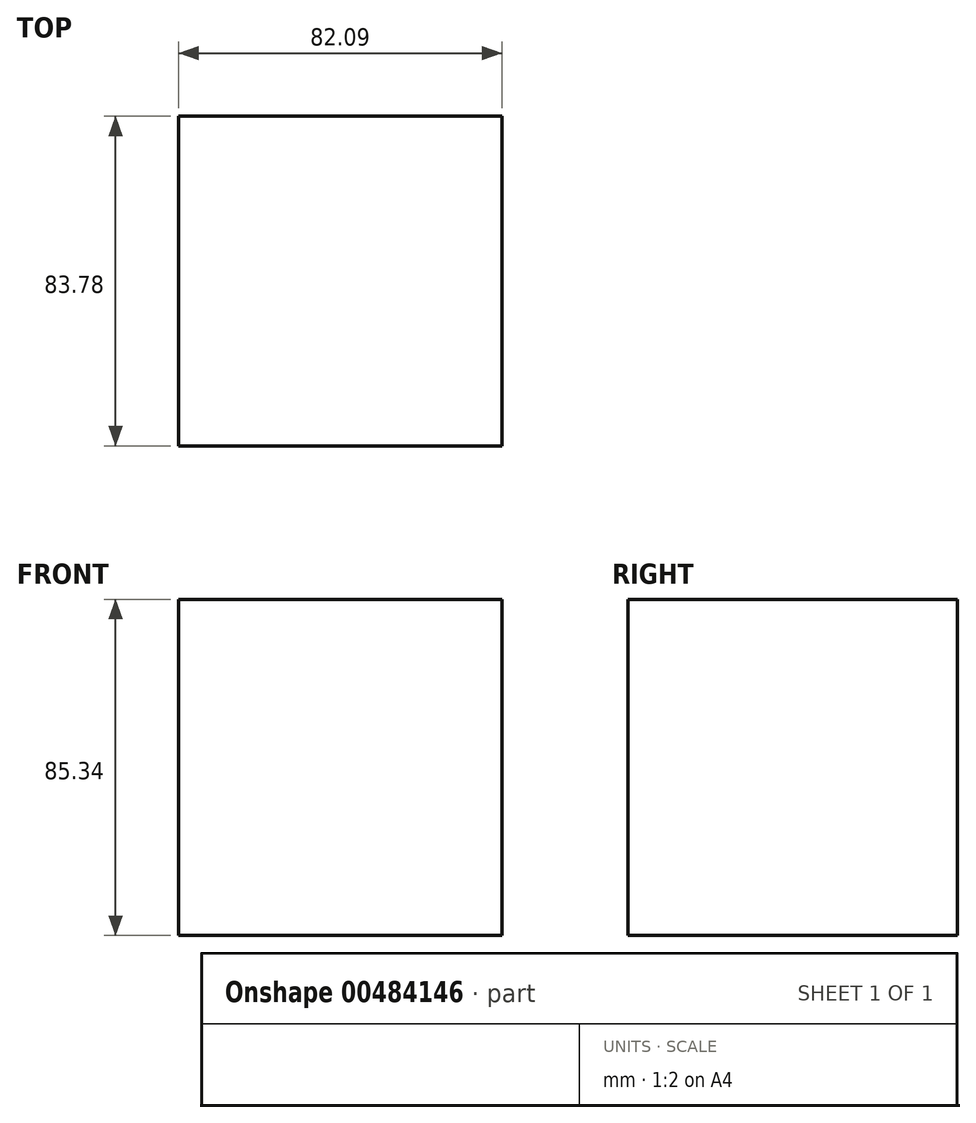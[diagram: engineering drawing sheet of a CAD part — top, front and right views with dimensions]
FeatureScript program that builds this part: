
annotation { "Feature Type Name" : "Feature", "Feature Type Description" : "" }
export const myFeature = defineFeature(function(context is Context, id is Id, definition is map)
    precondition{}
    {
        {
            var Q0;
            Q0=qCreatedBy(makeId("Top.planeOp"),FACE);
            var sketch = newSketch(context, id + "F0", { "sketchPlane" : qUnion([Q0])});
            skLineSegment(sketch, "E0.bottom", {"start": v(-34.76, -46.25) * mm, "end": v(47.33, -46.25) * mm});
            skLineSegment(sketch, "E0.top", {"start": v(-34.76, 37.53) * mm, "end": v(47.33, 37.53) * mm});
            skLineSegment(sketch, "E0.left", {"start": v(-34.76, -46.25) * mm, "end": v(-34.76, 37.53) * mm});
            skLineSegment(sketch, "E0.right", {"start": v(47.33, -46.25) * mm, "end": v(47.33, 37.53) * mm});
            skLineSegment(sketch, "E1.bottom", {"start": v(47.33, 37.53) * mm, "end": v(-16.75, 37.53) * mm});
            skLineSegment(sketch, "E1.top", {"start": v(47.33, 158.52) * mm, "end": v(-16.75, 158.52) * mm});
            skLineSegment(sketch, "E1.left", {"start": v(47.33, 37.53) * mm, "end": v(47.33, 158.52) * mm});
            skLineSegment(sketch, "E1.right", {"start": v(-16.75, 37.53) * mm, "end": v(-16.75, 158.52) * mm});
            skSolve(sketch);
        }
        {
            var Q0;
            Q0=makeQuery(id+"F0.imprint","IMPRINT",FACE,{"disambiguationData":[TD([[makeQuery(id+"F0.imprint","IMPRINT",EDGE,{"derivedFrom":sQuery(id+"F0.wireOp",EDGE,"E0.bottom")}),1.0]])]});
            extrude(context, id + "F1", {"entities" : qUnion([Q0]), "depth" : 85.34 * mm});
        }
    });
